# Revit family: metris_select_single_lever_kitchen_mixer_260_14847000
name_source: partatom
category: Plumbing Fixtures
revit_build: Autodesk Revit 2015 (Build: 20140903_1530(x64)
units: mm (PartAtom-declared; Revit-internal decimal feet)

## types (1)
- Chrome 000
    BIMobject category = Taps & Mixers
    BOSUseNativeGeometries = 1
    Brand url = http://www.hansgrohe-int.com
    Default Elevation = 4' - 0"
    Design country = Germany
    EAN code = https://4011097823676
    Edition number = 1
    IFC Classification = Valve
    Installation instructions = https://pro.hansgrohe-int.com
    Manufacturer country = Germany
    Manufacturer name = hansgrohe
    Masterformat 2014 Code = 22 41 39
    Masterformat 2014 Description = Residential Faucets, Supplies, and Trim
    Material main = Chrome
    NBS Reference Code = 35-79-79
    NBS Reference Description = Sink Water Supply Fittings
    Nominal height = 0
    Nominal width = 0
    OmniClass Code = 23-27 31 29 15
    OmniClass Description = Thermostatically Controlled Mixing Valves
    Product Guid = f947f8e2-64a0-4f28-8b16-dc56cd9d93d2
    Product SKU = 14847000
    Product data url = https://bimobject.com
    Product family = Metris Select
    Product group = Kitchen mixers
    Product name = Metris Select Single lever kitchen mixer 260 14847000
    Product url = https://pro.hansgrohe-int.com
    QR code = http://bimobject.com
    Technical description = https://pro.hansgrohe-int.com
    UNSPSC Code = 401416
    Uniclass 1.4 Code = L7117
    Uniclass 1.4 Description = Valves for water supply/distribution
    Uniclass 2.0 Code = PR-94-94-xx
    Uniclass 2.0 Description = Thermostatic Mixing Valves
    Uniclass 2015 Code = Pr_40_20_87_84
    Uniclass 2015 Name = Sink taps
    Uniformat II Code = D2010
    Uniformat II Description = Plumbing Fixtures
    Weight Net (Kg) = 0

## geometry (parser evidence)
native form markers: Sweep x2
no freeform markers — native parametric forms only
